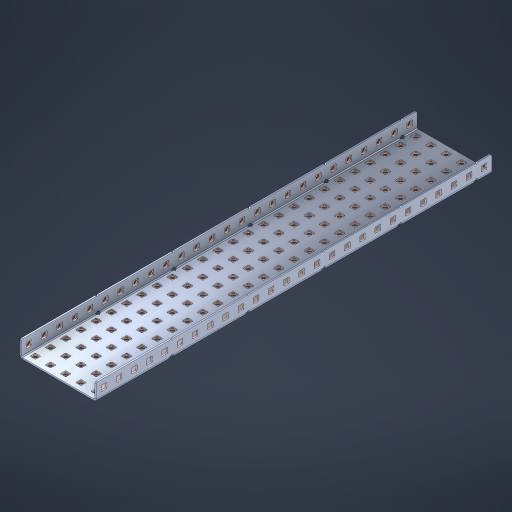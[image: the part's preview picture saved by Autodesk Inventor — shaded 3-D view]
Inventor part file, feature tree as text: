
AUTODESK INVENTOR PART (.ipt)
format: ipt  version: 2023 (Build 270158000, 158)  size: 2,044,416 bytes
history: native  units: in
note: dims shown in document units (in); Inventor stores cm internally (conversion verified against a paired STEP export)
features: other x187, extrude x181, sheet_metal_op x10, sketch x8, mirror x1, pattern_linear x1, chamfer x1
ambient origin geometry x8: Origin, YZ Plane, XZ Plane, XY Plane, X Axis, Y Axis, Z Axis, Center Point
bodies: Solid1 (feature_tree), Body (feature_tree)
feature tree (389):
  other  "Flange Pattern Plane"
  sheet_metal_op  "Flange Pattern"
  sheet_metal_op  "Body Pattern"
  other  "Arc Length"
  mirror  "Notch Mirror"
  pattern_linear  "Notch Pattern"  Spacing1=0.1875in  [1 undecoded]
  chamfer  "End Chamfer"
  extrude  "Half Cut"  Depth=0.0469in
  sketch  "Sketch1"  dims[d0=2.5in]
  other  "Plate1"
  sketch  "Sketch2"  dims[d1=13.0in]
  other  "Plate2"
  sheet_metal_op  "Bend1"
  sheet_metal_op  "Corner1"
  sketch  "Sketch3"  dims[d2=0.0469in]
  other  "Flange Pattern Sketch"
  sketch  "Sketch7"  dims[d3=0.0469in]
  other  "Srf1"
  other  "Srf2"
  sketch  "Sketch8"  dims[d4=0.0234in]
  sketch  "Sketch9"  dims[d5=0.0938in]
  other  "Srf91"
  sheet_metal_op  "Body Pattern Sketch"
  other  "Srf92"
  sketch  "Sketch13"  dims[d6=0.0469in]
  sketch  "Sketch14"  dims[d7=0.5in d8=90.0deg d9=0.0312in d10=0.1875in d11=0.0469in d12=0.0469in d16=0.182in d17=0.02in d18=0.0469in d19=0.0in d20=0.25in d21=0.25in d46=0.172in d47=1.0in d48=0.0in d49=0.182in d50=0.02in d51=0.25in d52=0.25in d53=0.0469in d54=0.0in d55=0.172in d56=1.0in d57=0.0in d60=10.2362in d62=0.5in d63=1.9685in d65=0.5in d85=0.1227in d86=0.1659in d88=0.04in d89=0.0469in d90=0.0in d91=0.04in d92=0.0491in d95=2.5in d96=0.04in d97=0.25in d98=45.0deg d101=0.0in d102=2.497in d131=2.5in d132=10.2362in d134=0.5in d139=0.5in]
  other  "Srf856"
  other  "Srf1310"
  other  "Srf1311"
  other  "Srf1312"
  other  "Srf1376"
  other  "Srf1377"
  other  "Srf1728"
  other  "Srf1755"
  other  "Srf1878"
  other  "Srf1879"
  other  "Srf1880"
  other  "Srf1881"
  other  "Srf1882"
  other  "Srf1883"
  other  "Srf1884"
  other  "Srf1885"
  other  "Srf1886"
  other  "Srf1887"
  other  "Srf1888"
  other  "Srf1889"
  other  "Srf1890"
  other  "Srf1891"
  other  "Srf1892"
  other  "Srf1893"
  other  "Srf1894"
  other  "Srf1895"
  other  "Srf1896"
  other  "Srf1897"
  other  "Srf1898"
  other  "Srf1899"
  other  "Srf1900"
  other  "Srf1901"
  other  "Srf1902"
  other  "Srf1903"
  other  "Srf1904"
  other  "Srf1905"
  other  "Srf1906"
  other  "Srf1942"
  other  "Srf1943"
  other  "Srf1944"
  other  "Srf1945"
  other  "Srf1946"
  other  "Srf1947"
  other  "Srf1948"
  other  "Srf1949"
  other  "Srf1950"
  other  "Srf1951"
  other  "Srf1952"
  other  "Srf1953"
  other  "Srf1954"
  other  "Srf1955"
  other  "Srf1956"
  other  "Srf1957"
  other  "Srf1958"
  other  "Srf1959"
  other  "Srf1960"
  other  "Srf1961"
  other  "Srf1962"
  other  "Srf1963"
  other  "Srf1964"
  other  "Srf1965"
  other  "Srf1966"
  other  "Srf1967"
  other  "Srf1968"
  other  "Srf1969"
  other  "Srf1970"
  other  "Srf2111"
  other  "Srf2112"
  other  "Srf2113"
  other  "Srf2114"
  other  "Srf2115"
  other  "Srf2116"
  other  "Srf2117"
  other  "Srf2118"
  other  "Srf2119"
  other  "Srf2120"
  other  "Srf2121"
  other  "Srf2122"
  other  "Srf2123"
  other  "Srf2124"
  other  "Srf2125"
  other  "Srf2126"
  other  "Srf2127"
  other  "Srf2146"
  other  "Srf2147"
  other  "Srf2148"
  other  "Srf2149"
  other  "Srf2150"
  other  "Srf2151"
  other  "Srf2152"
  other  "Srf2153"
  other  "Srf2154"
  other  "Srf2155"
  other  "Srf2156"
  other  "Srf2157"
  other  "Srf2158"
  other  "Srf2159"
  other  "Srf2160"
  other  "Srf2161"
  other  "Srf2162"
  other  "Srf2163"
  other  "Srf2164"
  other  "Srf2165"
  other  "Srf2166"
  other  "Srf2167"
  other  "Srf2168"
  other  "Srf2169"
  other  "Srf2170"
  other  "Srf2171"
  other  "Srf2172"
  other  "Srf2173"
  other  "Srf2174"
  other  "Srf2175"
  other  "Srf2176"
  other  "Srf2177"
  other  "Srf2178"
  other  "Srf2179"
  other  "Srf2180"
  other  "Srf2181"
  other  "Srf2182"
  other  "Srf2183"
  other  "Srf2184"
  other  "Srf2185"
  other  "Srf2186"
  other  "Srf2187"
  other  "Srf2188"
  other  "Srf2189"
  other  "Srf2190"
  other  "Srf2191"
  other  "Srf2192"
  other  "Srf2193"
  other  "Srf2194"
  other  "Srf2195"
  other  "Srf2196"
  other  "Srf2197"
  other  "Srf2198"
  other  "Srf2199"
  other  "Srf2200"
  other  "Srf2201"
  other  "Srf2202"
  other  "Srf2203"
  other  "Srf2204"
  other  "Srf2205"
  other  "Srf2206"
  other  "Srf2207"
  other  "Srf2208"
  other  "Srf2209"
  other  "Srf2210"
  other  "Srf2211"
  other  "Srf2212"
  other  "Srf2213"
  other  "Srf2214"
  other  "Srf2215"
  other  "Srf2216"
  other  "Srf2217"
  other  "Srf2218"
  other  "Srf2219"
  other  "Srf2220"
  other  "Srf2221"
  other  "Srf2222"
  other  "Srf2223"
  other  "Srf2224"
  other  "Srf2225"
  other  "Srf2226"
  other  "Srf2227"
  other  "Srf2228"
  other  "Srf2229"
  other  "Srf2230"
  other  "Srf2231"
  other  "Srf2232"
  other  "Srf2233"
  other  "Srf2234"
  other  "Srf2235"
  other  "Srf2236"
  other  "Srf2237"
  other  "Srf2238"
  other  "Srf2239"
  other  "Srf2240"
  sheet_metal_op  "Flange Stamp"
  sheet_metal_op  "Flange Circle"
  sheet_metal_op  "Body Stamp"
  sheet_metal_op  "Body Circle"
  sheet_metal_op  "Notch"
  extrude  "ExtrusionSrf2"  Depth=0.0469in
  extrude  "ExtrusionSrf92"  Depth=2.5in
  extrude  "ExtrusionSrf856"  Depth=0.02in
  extrude  "ExtrusionSrf1310"  Depth=0.0469in
  extrude  "ExtrusionSrf1311"  TaperAngle=0.0deg  [1 undecoded]
  extrude  "ExtrusionSrf1312"  Depth=0.25in
  extrude  "ExtrusionSrf1376"  Depth=0.25in
  extrude  "ExtrusionSrf1377"  Depth=2.5in
  extrude  "ExtrusionSrf1728"  Depth=2.5in TaperAngle=0.0deg
  extrude  "ExtrusionSrf1755"  Depth=2.5in
  extrude  "ExtrusionSrf1878"  Depth=0.02in
  extrude  "ExtrusionSrf1879"  Depth=0.25in
  extrude  "ExtrusionSrf1880"  Depth=0.25in
  extrude  "ExtrusionSrf1881"  Depth=0.0469in
  extrude  "ExtrusionSrf1882"  TaperAngle=0.0deg  [1 undecoded]
  extrude  "ExtrusionSrf1883"  Depth=2.5in
  extrude  "ExtrusionSrf1884"  Depth=2.5in TaperAngle=0.0deg
  extrude  "ExtrusionSrf1885"  Depth=2.5in
  extrude  "ExtrusionSrf1886"  Depth=2.5in
  extrude  "ExtrusionSrf1887"  Depth=2.5in
  extrude  "ExtrusionSrf1888"  Depth=2.5in
  extrude  "ExtrusionSrf1889"  Depth=2.5in
  extrude  "ExtrusionSrf1890"  Depth=0.0469in
  extrude  "ExtrusionSrf1891"  TaperAngle=0.0deg  [1 undecoded]
  extrude  "ExtrusionSrf1892"  Depth=2.5in
  extrude  "ExtrusionSrf1893"  Depth=2.5in
  extrude  "ExtrusionSrf1894"  Depth=2.5in
  extrude  "ExtrusionSrf1895"  Depth=0.25in TaperAngle=45.0deg
  extrude  "ExtrusionSrf1896"  TaperAngle=0.0deg  [1 undecoded]
  extrude  "ExtrusionSrf1897"  Depth=2.5in
  extrude  "ExtrusionSrf1898"  Depth=2.5in
  extrude  "ExtrusionSrf1899"  Depth=2.5in
  extrude  "ExtrusionSrf1900"  Depth=2.5in
  extrude  "ExtrusionSrf1901"  Depth=2.5in
  extrude  "ExtrusionSrf1902"  [1 undecoded]
  extrude  "ExtrusionSrf1903"  [1 undecoded]
  extrude  "ExtrusionSrf1904"  [1 undecoded]
  extrude  "ExtrusionSrf1905"  [1 undecoded]
  extrude  "ExtrusionSrf1906"  [1 undecoded]
  extrude  "ExtrusionSrf1942"  [1 undecoded]
  extrude  "ExtrusionSrf1943"  [1 undecoded]
  extrude  "ExtrusionSrf1944"  [1 undecoded]
  extrude  "ExtrusionSrf1945"  [1 undecoded]
  extrude  "ExtrusionSrf1946"  [1 undecoded]
  extrude  "ExtrusionSrf1947"  [1 undecoded]
  extrude  "ExtrusionSrf1948"  [1 undecoded]
  extrude  "ExtrusionSrf1949"  [1 undecoded]
  extrude  "ExtrusionSrf1950"  [1 undecoded]
  extrude  "ExtrusionSrf1951"  [1 undecoded]
  extrude  "ExtrusionSrf1952"  [1 undecoded]
  extrude  "ExtrusionSrf1953"  [1 undecoded]
  extrude  "ExtrusionSrf1954"  [1 undecoded]
  extrude  "ExtrusionSrf1955"  [1 undecoded]
  extrude  "ExtrusionSrf1956"  [1 undecoded]
  extrude  "ExtrusionSrf1957"  [1 undecoded]
  extrude  "ExtrusionSrf1958"  [1 undecoded]
  extrude  "ExtrusionSrf1959"  [1 undecoded]
  extrude  "ExtrusionSrf1960"  [1 undecoded]
  extrude  "ExtrusionSrf1961"  [1 undecoded]
  extrude  "ExtrusionSrf1962"  [1 undecoded]
  extrude  "ExtrusionSrf1963"  [1 undecoded]
  extrude  "ExtrusionSrf1964"  [1 undecoded]
  extrude  "ExtrusionSrf1965"  [1 undecoded]
  extrude  "ExtrusionSrf1966"  [1 undecoded]
  extrude  "ExtrusionSrf1967"  [1 undecoded]
  extrude  "ExtrusionSrf1968"  [1 undecoded]
  extrude  "ExtrusionSrf1969"  [1 undecoded]
  extrude  "ExtrusionSrf1970"  [1 undecoded]
  extrude  "ExtrusionSrf2111"  [1 undecoded]
  extrude  "ExtrusionSrf2112"  [1 undecoded]
  extrude  "ExtrusionSrf2113"  [1 undecoded]
  extrude  "ExtrusionSrf2114"  [1 undecoded]
  extrude  "ExtrusionSrf2115"  [1 undecoded]
  extrude  "ExtrusionSrf2116"  [1 undecoded]
  extrude  "ExtrusionSrf2117"  [1 undecoded]
  extrude  "ExtrusionSrf2118"  [1 undecoded]
  extrude  "ExtrusionSrf2119"  [1 undecoded]
  extrude  "ExtrusionSrf2120"  [1 undecoded]
  extrude  "ExtrusionSrf2121"  [1 undecoded]
  extrude  "ExtrusionSrf2122"  [1 undecoded]
  extrude  "ExtrusionSrf2123"  [1 undecoded]
  extrude  "ExtrusionSrf2124"  [1 undecoded]
  extrude  "ExtrusionSrf2125"  [1 undecoded]
  extrude  "ExtrusionSrf2126"  [1 undecoded]
  extrude  "ExtrusionSrf2127"  [1 undecoded]
  extrude  "ExtrusionSrf2146"  [1 undecoded]
  extrude  "ExtrusionSrf2147"  [1 undecoded]
  extrude  "ExtrusionSrf2148"  [1 undecoded]
  extrude  "ExtrusionSrf2149"  [1 undecoded]
  extrude  "ExtrusionSrf2150"  [1 undecoded]
  extrude  "ExtrusionSrf2151"  [1 undecoded]
  extrude  "ExtrusionSrf2152"  [1 undecoded]
  extrude  "ExtrusionSrf2153"  [1 undecoded]
  extrude  "ExtrusionSrf2154"  [1 undecoded]
  extrude  "ExtrusionSrf2155"  [1 undecoded]
  extrude  "ExtrusionSrf2156"  [1 undecoded]
  extrude  "ExtrusionSrf2157"  [1 undecoded]
  extrude  "ExtrusionSrf2158"  [1 undecoded]
  extrude  "ExtrusionSrf2159"  [1 undecoded]
  extrude  "ExtrusionSrf2160"  [1 undecoded]
  extrude  "ExtrusionSrf2161"  [1 undecoded]
  extrude  "ExtrusionSrf2162"  [1 undecoded]
  extrude  "ExtrusionSrf2163"  [1 undecoded]
  extrude  "ExtrusionSrf2164"  [1 undecoded]
  extrude  "ExtrusionSrf2165"  [1 undecoded]
  extrude  "ExtrusionSrf2166"  [1 undecoded]
  extrude  "ExtrusionSrf2167"  [1 undecoded]
  extrude  "ExtrusionSrf2168"  [1 undecoded]
  extrude  "ExtrusionSrf2169"  [1 undecoded]
  extrude  "ExtrusionSrf2170"  [1 undecoded]
  extrude  "ExtrusionSrf2171"  [1 undecoded]
  extrude  "ExtrusionSrf2172"  [1 undecoded]
  extrude  "ExtrusionSrf2173"  [1 undecoded]
  extrude  "ExtrusionSrf2174"  [1 undecoded]
  extrude  "ExtrusionSrf2175"  [1 undecoded]
  extrude  "ExtrusionSrf2176"  [1 undecoded]
  extrude  "ExtrusionSrf2177"  [1 undecoded]
  extrude  "ExtrusionSrf2178"  [1 undecoded]
  extrude  "ExtrusionSrf2179"  [1 undecoded]
  extrude  "ExtrusionSrf2180"  [1 undecoded]
  extrude  "ExtrusionSrf2181"  [1 undecoded]
  extrude  "ExtrusionSrf2182"  [1 undecoded]
  extrude  "ExtrusionSrf2183"  [1 undecoded]
  extrude  "ExtrusionSrf2184"  [1 undecoded]
  extrude  "ExtrusionSrf2185"  [1 undecoded]
  extrude  "ExtrusionSrf2186"  [1 undecoded]
  extrude  "ExtrusionSrf2187"  [1 undecoded]
  extrude  "ExtrusionSrf2188"  [1 undecoded]
  extrude  "ExtrusionSrf2189"  [1 undecoded]
  extrude  "ExtrusionSrf2190"  [1 undecoded]
  extrude  "ExtrusionSrf2191"  [1 undecoded]
  extrude  "ExtrusionSrf2192"  [1 undecoded]
  extrude  "ExtrusionSrf2193"  [1 undecoded]
  extrude  "ExtrusionSrf2194"  [1 undecoded]
  extrude  "ExtrusionSrf2195"  [1 undecoded]
  extrude  "ExtrusionSrf2196"  [1 undecoded]
  extrude  "ExtrusionSrf2197"  [1 undecoded]
  extrude  "ExtrusionSrf2198"  [1 undecoded]
  extrude  "ExtrusionSrf2199"  [1 undecoded]
  extrude  "ExtrusionSrf2200"  [1 undecoded]
  extrude  "ExtrusionSrf2201"  [1 undecoded]
  extrude  "ExtrusionSrf2202"  [1 undecoded]
  extrude  "ExtrusionSrf2203"  [1 undecoded]
  extrude  "ExtrusionSrf2204"  [1 undecoded]
  extrude  "ExtrusionSrf2205"  [1 undecoded]
  extrude  "ExtrusionSrf2206"  [1 undecoded]
  extrude  "ExtrusionSrf2207"  [1 undecoded]
  extrude  "ExtrusionSrf2208"  [1 undecoded]
  extrude  "ExtrusionSrf2209"  [1 undecoded]
  extrude  "ExtrusionSrf2210"  [1 undecoded]
  extrude  "ExtrusionSrf2211"  [1 undecoded]
  extrude  "ExtrusionSrf2212"  [1 undecoded]
  extrude  "ExtrusionSrf2213"  [1 undecoded]
  extrude  "ExtrusionSrf2214"  [1 undecoded]
  extrude  "ExtrusionSrf2215"  [1 undecoded]
  extrude  "ExtrusionSrf2216"  [1 undecoded]
  extrude  "ExtrusionSrf2217"  [1 undecoded]
  extrude  "ExtrusionSrf2218"  [1 undecoded]
  extrude  "ExtrusionSrf2219"  [1 undecoded]
  extrude  "ExtrusionSrf2220"  [1 undecoded]
  extrude  "ExtrusionSrf2221"  [1 undecoded]
  extrude  "ExtrusionSrf2222"  [1 undecoded]
  extrude  "ExtrusionSrf2223"  [1 undecoded]
  extrude  "ExtrusionSrf2224"  [1 undecoded]
  extrude  "ExtrusionSrf2225"  [1 undecoded]
  extrude  "ExtrusionSrf2226"  [1 undecoded]
  extrude  "ExtrusionSrf2227"  [1 undecoded]
  extrude  "ExtrusionSrf2228"  [1 undecoded]
  extrude  "ExtrusionSrf2229"  [1 undecoded]
  extrude  "ExtrusionSrf2230"  [1 undecoded]
  extrude  "ExtrusionSrf2231"  [1 undecoded]
  extrude  "ExtrusionSrf2232"  [1 undecoded]
  extrude  "ExtrusionSrf2233"  [1 undecoded]
  extrude  "ExtrusionSrf2234"  [1 undecoded]
  extrude  "ExtrusionSrf2235"  [1 undecoded]
  extrude  "ExtrusionSrf2236"  [1 undecoded]
  extrude  "ExtrusionSrf2237"  [1 undecoded]
  extrude  "ExtrusionSrf2238"  [1 undecoded]
  extrude  "ExtrusionSrf2239"  [1 undecoded]
  extrude  "ExtrusionSrf2240"  [1 undecoded]
note: 151 required parameter values undecoded (feature->parameter linkage not recoverable at this tier; creation-order binding heuristic only, values carry confidence <= 0.55)
